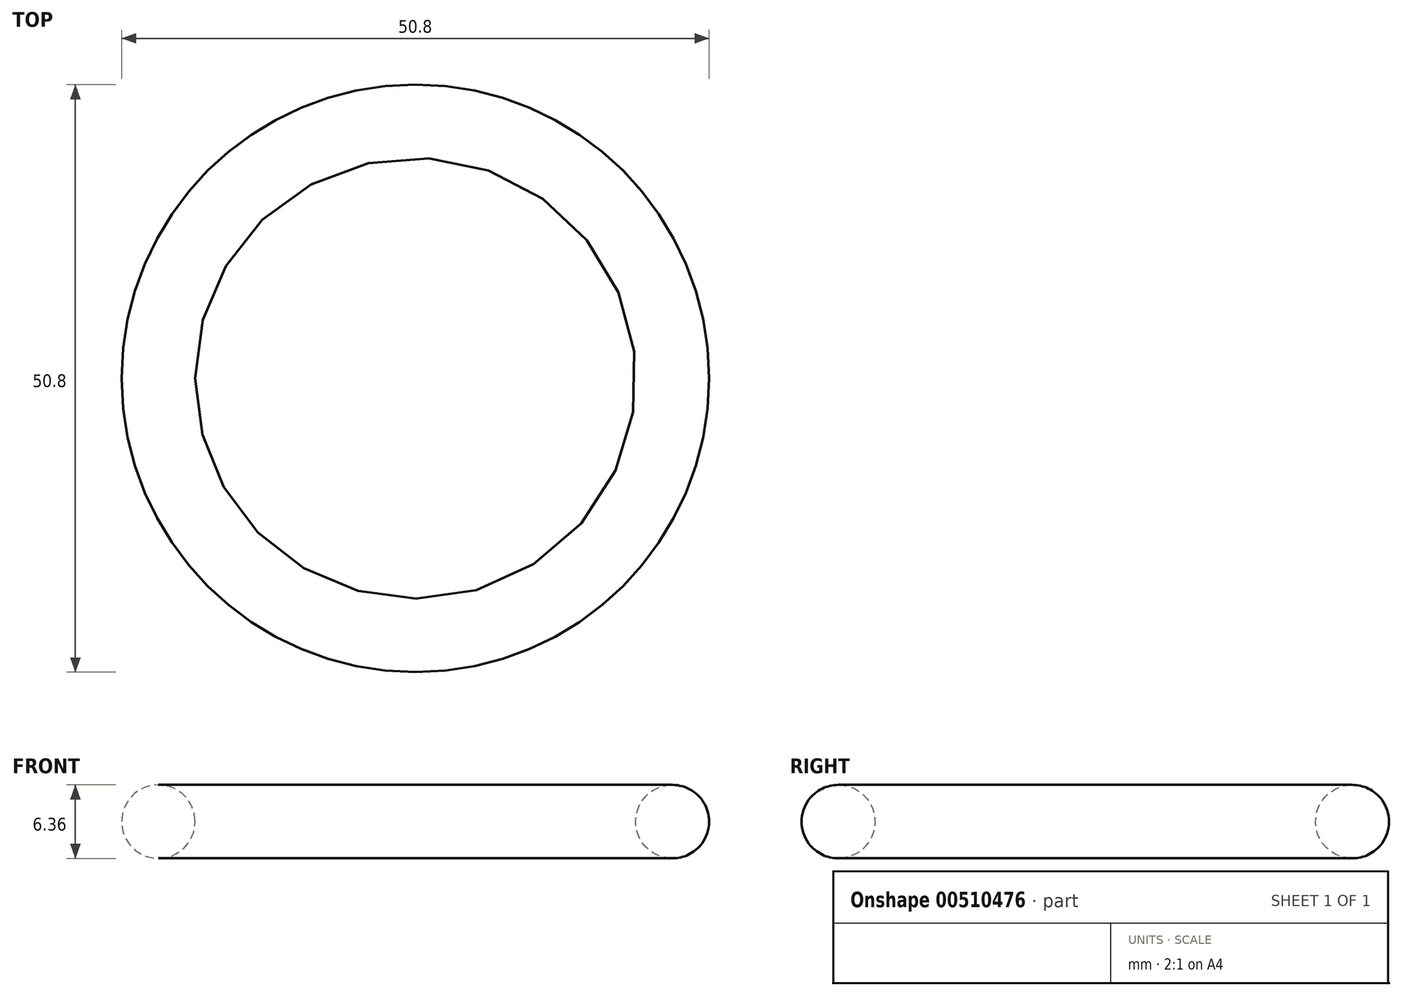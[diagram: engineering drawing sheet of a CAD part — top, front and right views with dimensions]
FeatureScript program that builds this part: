
annotation { "Feature Type Name" : "Feature", "Feature Type Description" : "" }
export const myFeature = defineFeature(function(context is Context, id is Id, definition is map)
    precondition{}
    {
        {
            var Q0;
            Q0=qCreatedBy(makeId("Front.planeOp"),FACE);
            var sketch = newSketch(context, id + "F0", { "sketchPlane" : qUnion([Q0])});
            skCircle(sketch, "E0", {"center": v(-22.23, 0) * mm, "radius": 3.18 * mm});
            skLineSegment(sketch, "E1", {"start": v(0, 0) * mm, "end": v(0, 13.98) * mm, "construction": true});
            skSolve(sketch);
        }
        {
            var Q0;
            Q0 = qSketchRegion(id + "F0", true);
            var Q1;
            Q1=sQuery(id+"F0.wireOp",EDGE,"E1");
            revolve(context, id + "F1", {"entities" : qUnion([Q0]), "axis" : qUnion([Q1]), "revolveType" : RevolveType.FULL});
        }
    });
